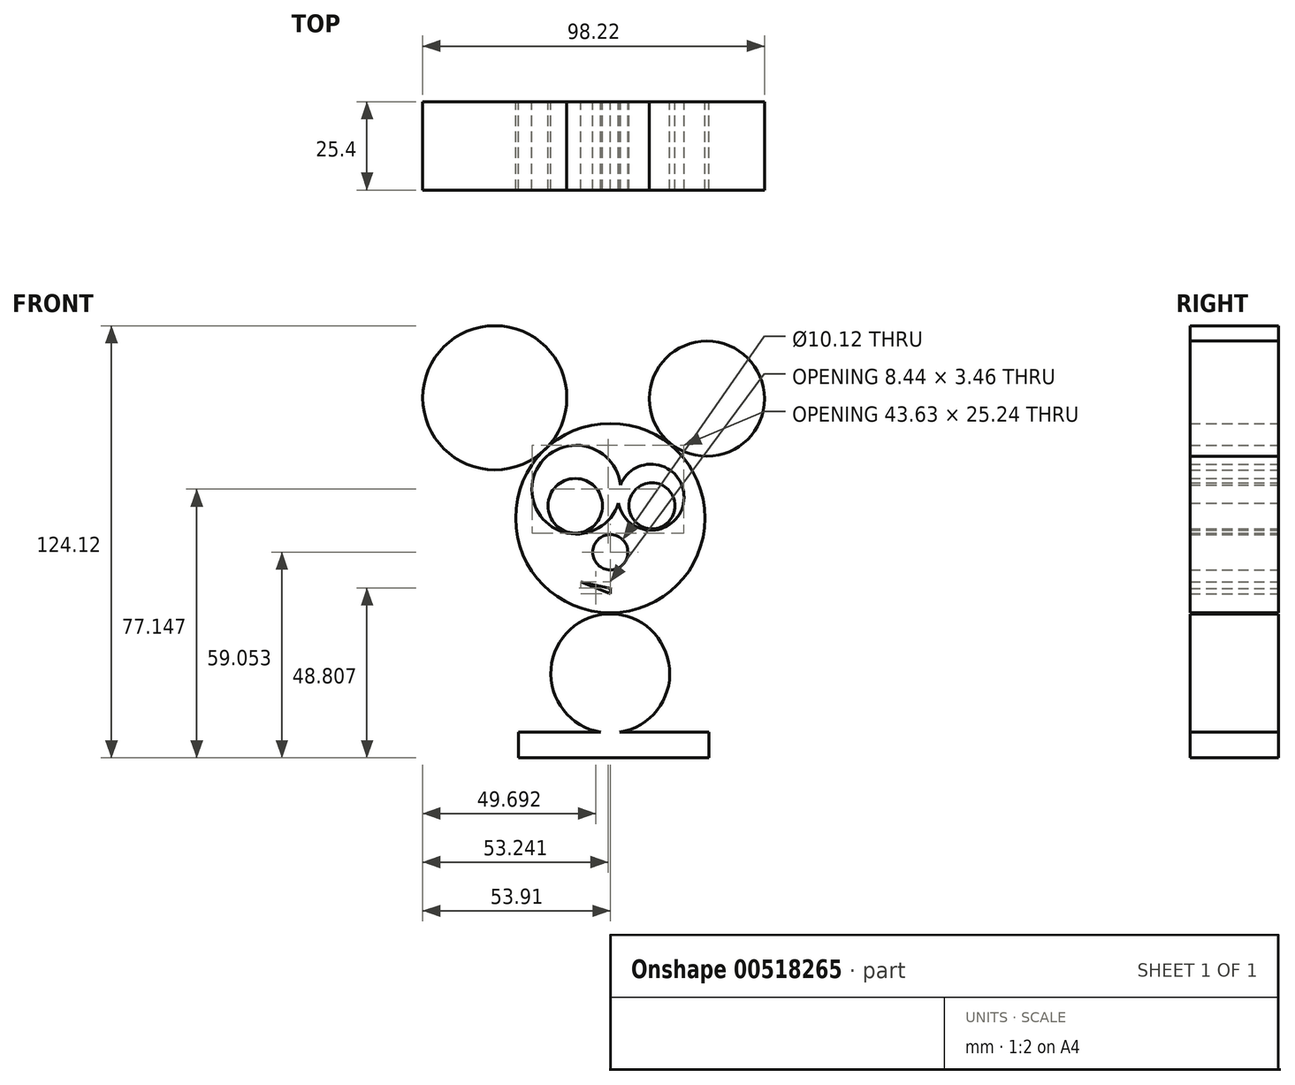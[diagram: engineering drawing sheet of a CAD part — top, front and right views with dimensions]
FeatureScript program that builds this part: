
annotation { "Feature Type Name" : "Feature", "Feature Type Description" : "" }
export const myFeature = defineFeature(function(context is Context, id is Id, definition is map)
    precondition{}
    {
        {
            var Q0;
            Q0=qCreatedBy(makeId("Front.planeOp"),FACE);
            var sketch = newSketch(context, id + "F0", { "sketchPlane" : qUnion([Q0])});
            skCircle(sketch, "E0", {"center": v(0, 0) * mm, "radius": 27.21 * mm});
            skCircle(sketch, "E1", {"center": v(-9.8, 8.16) * mm, "radius": 12.75 * mm});
            skCircle(sketch, "E2", {"center": v(11.7, 5.99) * mm, "radius": 9.5 * mm});
            skCircle(sketch, "E3", {"center": v(-33.2, 34.56) * mm, "radius": 20.71 * mm});
            skCircle(sketch, "E4", {"center": v(27.76, 34.3) * mm, "radius": 16.56 * mm});
            skCircle(sketch, "E5", {"center": v(0, -44.63) * mm, "radius": 17.1 * mm});
            skCircle(sketch, "E6", {"center": v(0, -9.8) * mm, "radius": 5.06 * mm});
            skLineSegment(sketch, "E7", {"start": v(0, -14.86) * mm, "end": v(0, -21.77) * mm});
            skLineSegment(sketch, "E8", {"start": v(0, -21.77) * mm, "end": v(-8.44, -18.32) * mm});
            skPoint(sketch, "E8.endSnap0", {"position": v(0, -18.32) * mm});
            skLineSegment(sketch, "E9", {"start": v(-8.44, -18.32) * mm, "end": v(7.08, -21.77) * mm});
            skSolve(sketch);
        }
        {
            var Q0;
            Q0 = qSketchRegion(id + "F0", true);
            extrude(context, id + "F1", {"entities" : qUnion([Q0]), "depth" : 25.4 * mm, "offsetDistance" : 25.4 * mm});
        }
        {
            var Q0;
            Q0=qCreatedBy(makeId("Front.planeOp"),FACE);
            var sketch = newSketch(context, id + "F2", { "sketchPlane" : qUnion([Q0])});
            skLineSegment(sketch, "E10", {"start": v(-26.4, -61.5) * mm, "end": v(28.3, -61.5) * mm});
            skLineSegment(sketch, "E11", {"start": v(28.3, -61.5) * mm, "end": v(28.3, -68.85) * mm});
            skLineSegment(sketch, "E12", {"start": v(28.3, -68.85) * mm, "end": v(-26.4, -68.85) * mm});
            skLineSegment(sketch, "E13", {"start": v(-26.4, -68.85) * mm, "end": v(-26.4, -61.5) * mm});
            skLineSegment(sketch, "E14.0.1.0", {"start": v(28.45, -68.83) * mm, "end": v(28.45, -61.49) * mm});
            skLineSegment(sketch, "E14.1.0.0", {"start": v(-1, -68.85) * mm, "end": v(-1, -61.5) * mm});
            skLineSegment(sketch, "E14.1.1.0", {"start": v(53.85, -68.83) * mm, "end": v(53.85, -61.49) * mm});
            skLineSegment(sketch, "E14.2.0.0", {"start": v(24.4, -68.85) * mm, "end": v(24.4, -61.5) * mm});
            skLineSegment(sketch, "E14.2.1.0", {"start": v(79.25, -68.83) * mm, "end": v(79.25, -61.49) * mm});
            skLineSegment(sketch, "E14.direction1", {"start": v(-26.4, -68.85) * mm, "end": v(-1, -68.85) * mm, "construction": true});
            skLineSegment(sketch, "E14.direction2", {"start": v(-26.4, -68.85) * mm, "end": v(28.45, -68.83) * mm, "construction": true});
            skSolve(sketch);
        }
        {
            var Q0;
            Q0 = qSketchRegion(id + "F2", true);
            extrude(context, id + "F3", {"entities" : qUnion([Q0]), "operationType" : NewBodyOperationType.ADD, "depth" : 25.4 * mm, "offsetDistance" : 25.4 * mm});
        }
        {
            var Q0;
            Q0=qCreatedBy(makeId("Front.planeOp"),FACE);
            var sketch = newSketch(context, id + "F4", { "sketchPlane" : qUnion([Q0])});
            skCircle(sketch, "E15", {"center": v(-10.07, 3.54) * mm, "radius": 7.84 * mm});
            skCircle(sketch, "E16", {"center": v(11.97, 3.54) * mm, "radius": 6.64 * mm});
            skSolve(sketch);
        }
        {
            var Q0;
            Q0 = qSketchRegion(id + "F4", true);
            extrude(context, id + "F5", {"entities" : qUnion([Q0]), "depth" : 25.4 * mm, "offsetDistance" : 25.4 * mm});
        }
    });
